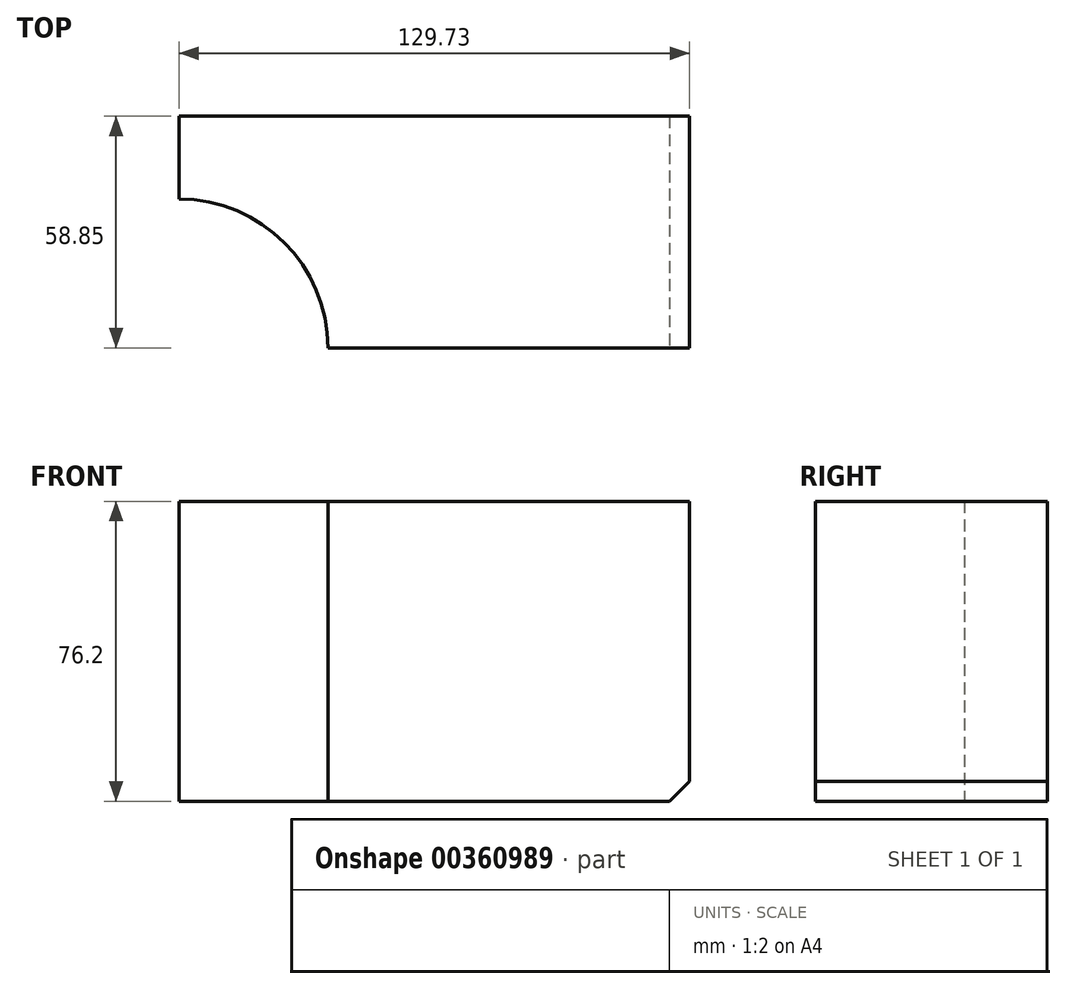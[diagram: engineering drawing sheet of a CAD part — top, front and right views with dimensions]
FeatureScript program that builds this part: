
annotation { "Feature Type Name" : "Feature", "Feature Type Description" : "" }
export const myFeature = defineFeature(function(context is Context, id is Id, definition is map)
    precondition{}
    {
        {
            var Q0;
            Q0=qCreatedBy(makeId("Top.planeOp"),FACE);
            var sketch = newSketch(context, id + "F0", { "sketchPlane" : qUnion([Q0])});
            skLineSegment(sketch, "E0.bottom", {"start": v(0, 0) * mm, "end": v(129.73, 0) * mm});
            skLineSegment(sketch, "E0.top", {"start": v(0, 58.85) * mm, "end": v(129.73, 58.85) * mm});
            skLineSegment(sketch, "E0.left", {"start": v(0, 0) * mm, "end": v(0, 58.85) * mm});
            skLineSegment(sketch, "E0.right", {"start": v(129.73, 0) * mm, "end": v(129.73, 58.85) * mm});
            skCircle(sketch, "E1", {"center": v(0, 0) * mm, "radius": 37.83 * mm});
            skSolve(sketch);
        }
        {
            var Q0;
            {var subQ2=sQuery(id+"F0.wireOp",EDGE,"E0.top");Q0=makeQuery(id+"F0.imprint","IMPRINT",FACE,{"disambiguationData":[TD([[makeQuery(id+"F0.imprint","IMPRINT",EDGE,{"derivedFrom":subQ2}),-1.0]])]});}
            extrude(context, id + "F1", {"entities" : qUnion([Q0]), "depth" : 76.2 * mm});
        }
        {
            var Q0;
            Q0=sQuery(id+"F0.wireOp",EDGE,"E1");
            extrude(context, id + "F2", {"bodyType" : ToolBodyType.SURFACE, "surfaceEntities" : qUnion([Q0]), "depth" : 76.2 * mm});
        }
        {
            var Q0;
            Q0=makeQuery(id+"F1.opExtrude","CAP_EDGE",EDGE,{"disambiguationData":[OSD([sQuery(id+"F0.wireOp",EDGE,"E0.right")])],"isStart":true});
            chamfer(context, id + "F3", {"entities" : qUnion([Q0]), "width" : 5.08 * mm, "tangentPropagation" : true});
        }
    });
